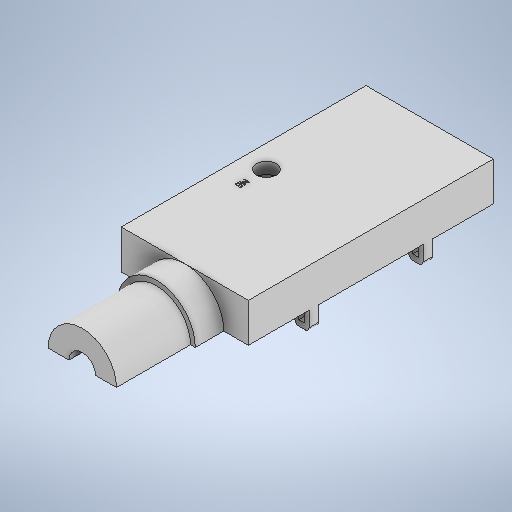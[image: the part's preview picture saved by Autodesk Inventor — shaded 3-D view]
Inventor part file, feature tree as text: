
AUTODESK INVENTOR PART (.ipt)
format: ipt  version: 2025 (Build 290162000, 162)  size: 393,216 bytes
history: native  units: mm
features: sketch x8, extrude x6, plane x2, mirror x1, hole x1, emboss x1, fillet x1
ambient origin geometry x8: Origin, YZ Plane, XZ Plane, XY Plane, X Axis, Y Axis, Z Axis, Center Point
bodies: Solid1 (feature_tree)
feature tree (20):
  extrude  "Extrusion1"  Depth=20.5mm
  extrude  "Extrusion2"  Depth=20.5mm
  extrude  "Extrusion3"  Depth=18.0mm
  extrude  "Extrusion5"  Depth=39.0mm TaperAngle=0.0deg
  plane  "Work Plane1"
  extrude  "Extrusion6"  TaperAngle=180.0deg  [1 undecoded]
  mirror  "Mirror1"
  hole  "Hole1"  [1 undecoded]
  emboss  "Emboss1"
  plane  "Work Plane2"
  extrude  "Extrusion7"  Depth=10.0mm TaperAngle=0.0deg
  fillet  "Fillet1"  Radius=12.0mm
  sketch  "Sketch1"  dims[d0=129.0mm d1=20.5mm]
  sketch  "Sketch2"  dims[d2=67.0mm d3=0.0mm d4=20.5mm]
  sketch  "Sketch3"  dims[d5=15.0mm d6=0.0mm d7=18.0mm]
  sketch  "Sketch5"  dims[d8=180.0deg d9=39.0mm d10=0.0mm]
  sketch  "Sketch6"  dims[d16=7.0mm d17=180.0deg]
  sketch  "Sketch7"  dims[d18=0.0mm d19=0.0mm d20=30.0mm]
  sketch  "Sketch8"  dims[d21=10.0mm d22=2.5mm d23=7.0mm d24=7.5mm d25=5.0mm d26=2.0mm d27=2.0mm d28=2.0mm d29=5.0mm d30=0.0mm]
  sketch  "Sketch10"  dims[d31=6.2mm d32=6.0mm d33=10.5mm d34=6.0mm d35=90.0deg d36=8.0mm d37=20.594885mm d38=12.0mm d39=1.0mm d40=0.0mm d41=-13.5mm d42=5.9mm d43=5.0mm d44=0.0mm d45=1.5mm]
note: 2 required parameter values undecoded (feature->parameter linkage not recoverable at this tier; creation-order binding heuristic only, values carry confidence <= 0.55)
